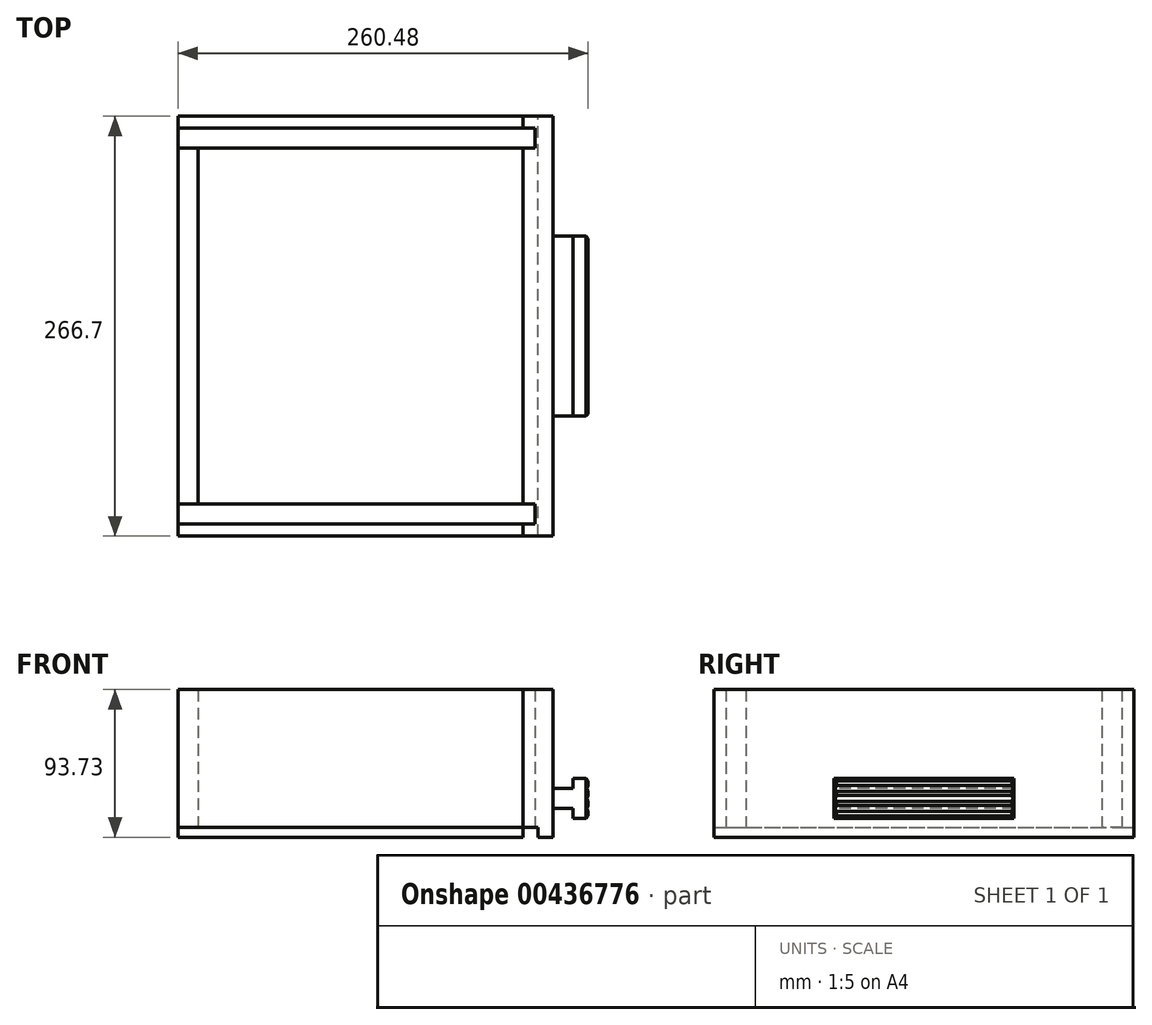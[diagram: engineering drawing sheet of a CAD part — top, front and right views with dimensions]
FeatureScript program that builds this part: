
annotation { "Feature Type Name" : "Feature", "Feature Type Description" : "" }
export const myFeature = defineFeature(function(context is Context, id is Id, definition is map)
    precondition{}
    {
        {
            var Q0;
            Q0=qCreatedBy(makeId("Top.planeOp"),FACE);
            var sketch = newSketch(context, id + "F0", { "sketchPlane" : qUnion([Q0])});
            skLineSegment(sketch, "E0.bottom", {"start": v(114.3, -133.35) * mm, "end": v(-114.3, -133.35) * mm});
            skLineSegment(sketch, "E0.top", {"start": v(114.3, 133.35) * mm, "end": v(-114.3, 133.35) * mm});
            skLineSegment(sketch, "E0.left", {"start": v(114.3, -133.35) * mm, "end": v(114.3, 133.35) * mm});
            skLineSegment(sketch, "E0.right", {"start": v(-114.3, -133.35) * mm, "end": v(-114.3, 133.35) * mm});
            skPoint(sketch, "E0.middle", {"position": v(0, 0) * mm});
            skSolve(sketch);
        }
        {
            var Q0;
            Q0 = qSketchRegion(id + "F0", true);
            extrude(context, id + "F1", {"entities" : qUnion([Q0]), "depth" : 6.35 * mm});
        }
        {
            var Q0;
            Q0=makeQuery(id+"F1.opExtrude","SWEPT_FACE",FACE,{"disambiguationData":[OSD([sQuery(id+"F0.wireOp",EDGE,"E0.left")])]});
            var sketch = newSketch(context, id + "F2", { "sketchPlane" : qUnion([Q0])});
            skLineSegment(sketch, "E1.bottom", {"start": v(-133.35, 0) * mm, "end": v(133.35, 0) * mm});
            skLineSegment(sketch, "E1.top", {"start": v(-133.35, 93.73) * mm, "end": v(133.35, 93.73) * mm});
            skLineSegment(sketch, "E1.left", {"start": v(-133.35, 0) * mm, "end": v(-133.35, 93.73) * mm});
            skLineSegment(sketch, "E1.right", {"start": v(133.35, 0) * mm, "end": v(133.35, 93.73) * mm});
            skSolve(sketch);
        }
        {
            var Q0;
            Q0 = qSketchRegion(id + "F2", true);
            extrude(context, id + "F3", {"entities" : qUnion([Q0]), "endBound" : BoundingType.SYMMETRIC, "depth" : 19.05 * mm});
        }
        {
            var Q0;
            Q0=makeQuery(id+"F3.opExtrude","CAP_FACE",FACE,{"disambiguationData":[OSD([sQuery(id+"F2.wireOp",EDGE,"E1.bottom"),sQuery(id+"F2.wireOp",EDGE,"E1.top"),sQuery(id+"F2.wireOp",EDGE,"E1.left"),sQuery(id+"F2.wireOp",EDGE,"E1.right")])],"isStart":true});
            var sketch = newSketch(context, id + "F4", { "sketchPlane" : qUnion([Q0])});
            skLineSegment(sketch, "E2.bottom", {"start": v(-125.73, 93.73) * mm, "end": v(-113.03, 93.73) * mm});
            skLineSegment(sketch, "E2.top", {"start": v(-125.73, 6.35) * mm, "end": v(-113.03, 6.35) * mm});
            skLineSegment(sketch, "E2.left", {"start": v(-125.73, 93.73) * mm, "end": v(-125.73, 6.35) * mm});
            skLineSegment(sketch, "E2.right", {"start": v(-113.03, 93.73) * mm, "end": v(-113.03, 6.35) * mm});
            skLineSegment(sketch, "E3.bottom", {"start": v(125.73, 93.73) * mm, "end": v(113.03, 93.73) * mm});
            skLineSegment(sketch, "E3.top", {"start": v(125.73, 6.35) * mm, "end": v(113.03, 6.35) * mm});
            skLineSegment(sketch, "E3.left", {"start": v(125.73, 93.73) * mm, "end": v(125.73, 6.35) * mm});
            skLineSegment(sketch, "E3.right", {"start": v(113.03, 93.73) * mm, "end": v(113.03, 6.35) * mm});
            skSolve(sketch);
        }
        {
            var Q0;
            Q0=makeQuery(id+"F4.imprint","IMPRINT",FACE,{"disambiguationData":[TD([[makeQuery(id+"F4.imprint","IMPRINT",EDGE,{"derivedFrom":sQuery(id+"F4.wireOp",EDGE,"E2.bottom")}),1.0]])]});
            var Q1;
            Q1=makeQuery(id+"F4.imprint","IMPRINT",FACE,{"disambiguationData":[TD([[makeQuery(id+"F4.imprint","IMPRINT",EDGE,{"derivedFrom":sQuery(id+"F4.wireOp",EDGE,"E3.bottom")}),1.0]])]});
            extrude(context, id + "F5", {"entities" : qUnion([Q0, Q1]), "operationType" : NewBodyOperationType.REMOVE, "oppositeDirection" : true, "depth" : 7.62 * mm});
        }
        {
            var Q0;
            Q0=makeQuery(id+"F3.opExtrude","SWEPT_FACE",FACE,{"disambiguationData":[OSD([sQuery(id+"F2.wireOp",EDGE,"E1.right")])]});
            var sketch = newSketch(context, id + "F6", { "sketchPlane" : qUnion([Q0])});
            skLineSegment(sketch, "E4.bottom", {"start": v(-114.3, 0) * mm, "end": v(-104.78, 0) * mm});
            skLineSegment(sketch, "E4.top", {"start": v(-114.3, 6.35) * mm, "end": v(-104.78, 6.35) * mm});
            skLineSegment(sketch, "E4.left", {"start": v(-114.3, 0) * mm, "end": v(-114.3, 6.35) * mm});
            skLineSegment(sketch, "E4.right", {"start": v(-104.78, 0) * mm, "end": v(-104.78, 6.35) * mm});
            skSolve(sketch);
        }
        {
            var Q0;
            Q0 = qSketchRegion(id + "F6", true);
            extrude(context, id + "F7", {"entities" : qUnion([Q0]), "operationType" : NewBodyOperationType.REMOVE, "endBound" : BoundingType.THROUGH_ALL, "oppositeDirection" : true, "depth" : 25.4 * mm});
        }
        {
            var Q0;
            Q0=makeQuery(id+"F5.boolean.opBoolean","COPY",FACE,{"derivedFrom":makeQuery(id+"F5.opExtrude","CAP_FACE",FACE,{"disambiguationData":[OSD([sQuery(id+"F4.wireOp",EDGE,"E2.bottom"),sQuery(id+"F4.wireOp",EDGE,"E2.top"),sQuery(id+"F4.wireOp",EDGE,"E2.left"),sQuery(id+"F4.wireOp",EDGE,"E2.right")])],"isStart":false})});
            var Q1;
            Q1=makeQuery(id+"F5.boolean.opBoolean","COPY",FACE,{"derivedFrom":makeQuery(id+"F5.opExtrude","CAP_FACE",FACE,{"disambiguationData":[OSD([sQuery(id+"F4.wireOp",EDGE,"E3.bottom"),sQuery(id+"F4.wireOp",EDGE,"E3.top"),sQuery(id+"F4.wireOp",EDGE,"E3.left"),sQuery(id+"F4.wireOp",EDGE,"E3.right")])],"isStart":false})});
            var Q2;
            Q2=makeQuery(id+"F1.opExtrude","SWEPT_FACE",FACE,{"disambiguationData":[OSD([sQuery(id+"F0.wireOp",EDGE,"E0.right")])]});
            extrude(context, id + "F8", {"entities" : qUnion([Q0, Q1]), "endBound" : BoundingType.UP_TO_SURFACE, "endBoundEntityFace" : qUnion([Q2]), "depth" : 25.4 * mm});
        }
        {
            var Q0;
            Q0=makeQuery(id+"F8.opExtrude","CAP_FACE",FACE,{"disambiguationData":[OSD([sQuery(id+"F4.wireOp",EDGE,"E2.bottom"),sQuery(id+"F4.wireOp",EDGE,"E2.top"),sQuery(id+"F4.wireOp",EDGE,"E2.left"),sQuery(id+"F4.wireOp",EDGE,"E2.right")])],"isStart":false});
            var sketch = newSketch(context, id + "F9", { "sketchPlane" : qUnion([Q0])});
            skLineSegment(sketch, "E5.bottom", {"start": v(-113.03, 6.35) * mm, "end": v(113.03, 6.35) * mm});
            skLineSegment(sketch, "E5.top", {"start": v(-113.03, 93.73) * mm, "end": v(113.03, 93.73) * mm});
            skLineSegment(sketch, "E5.left", {"start": v(-113.03, 6.35) * mm, "end": v(-113.03, 93.73) * mm});
            skLineSegment(sketch, "E5.right", {"start": v(113.03, 6.35) * mm, "end": v(113.03, 93.73) * mm});
            skLineSegment(sketch, "E6.0", {"start": v(113.03, 93.73) * mm, "end": v(113.03, 6.35) * mm});
            skSolve(sketch);
        }
        {
            var Q0;
            Q0 = qSketchRegion(id + "F9", true);
            extrude(context, id + "F10", {"entities" : qUnion([Q0]), "oppositeDirection" : true, "depth" : 12.7 * mm});
        }
        {
            var Q0;
            Q0=makeQuery(id+"F3.opExtrude","SWEPT_FACE",FACE,{"disambiguationData":[OSD([sQuery(id+"F2.wireOp",EDGE,"E1.left")])]});
            cPlane(context, id + "F11", {"entities" : qUnion([Q0]), "cplaneType" : CPlaneType.OFFSET, "offset" : 76.2 * mm, "oppositeDirection" : true, "width" : 152.4 * mm, "height" : 152.4 * mm});
        }
        {
            var Q0;
            Q0=qCreatedBy(id+"F11.planeOp",FACE);
            var sketch = newSketch(context, id + "F12", { "sketchPlane" : qUnion([Q0])});
            skLineSegment(sketch, "E7.0", {"start": v(123.82, 93.73) * mm, "end": v(123.82, 0) * mm});
            skLineSegment(sketch, "E8.bottom", {"start": v(123.82, 18.29) * mm, "end": v(136.52, 18.29) * mm});
            skLineSegment(sketch, "E8.top", {"start": v(123.82, 30.99) * mm, "end": v(136.52, 30.99) * mm});
            skLineSegment(sketch, "E8.left", {"start": v(123.82, 18.29) * mm, "end": v(123.82, 30.99) * mm});
            skLineSegment(sketch, "E8.right", {"start": v(136.52, 18.29) * mm, "end": v(136.52, 30.99) * mm});
            skLineSegment(sketch, "E9.bottom", {"start": v(136.52, 11.94) * mm, "end": v(146.18, 11.94) * mm});
            skLineSegment(sketch, "E9.top", {"start": v(136.52, 37.34) * mm, "end": v(146.18, 37.34) * mm});
            skLineSegment(sketch, "E9.left", {"start": v(136.52, 11.94) * mm, "end": v(136.52, 37.34) * mm});
            skLineSegment(sketch, "E9.right", {"start": v(146.18, 11.94) * mm, "end": v(146.18, 37.34) * mm});
            skSolve(sketch);
        }
        {
            var Q0;
            Q0 = qSketchRegion(id + "F12", true);
            extrude(context, id + "F13", {"entities" : qUnion([Q0]), "oppositeDirection" : true, "depth" : 114.3 * mm});
        }
        {
            var Q0;
            Q0=makeQuery(id+"F13.opExtrude","SWEPT_FACE",FACE,{"disambiguationData":[OSD([sQuery(id+"F12.wireOp",EDGE,"E9.right")])]});
            chamfer(context, id + "F14", {"entities" : qUnion([Q0]), "width" : 1.52 * mm, "tangentPropagation" : true});
        }
        {
            var Q0;
            Q0=makeQuery(id+"F13.opExtrude","CAP_FACE",FACE,{"disambiguationData":[OSD([sQuery(id+"F12.wireOp",EDGE,"E8.bottom"),sQuery(id+"F12.wireOp",EDGE,"E8.top"),sQuery(id+"F12.wireOp",EDGE,"E8.left"),sQuery(id+"F12.wireOp",EDGE,"E9.bottom"),sQuery(id+"F12.wireOp",EDGE,"E9.top"),sQuery(id+"F12.wireOp",EDGE,"E9.left"),sQuery(id+"F12.wireOp",EDGE,"E9.right")])],"isStart":true});
            var sketch = newSketch(context, id + "F15", { "sketchPlane" : qUnion([Q0])});
            skLineSegment(sketch, "E10.0", {"start": v(146.18, 35.81) * mm, "end": v(146.18, 13.46) * mm});
            skCircle(sketch, "E11", {"center": v(148.72, 30.99) * mm, "radius": 3.18 * mm});
            skCircle(sketch, "E12", {"center": v(148.72, 24.64) * mm, "radius": 3.18 * mm});
            skCircle(sketch, "E13", {"center": v(148.72, 18.29) * mm, "radius": 3.18 * mm});
            skSolve(sketch);
        }
        {
            var Q0;
            Q0 = qSketchRegion(id + "F15", true);
            extrude(context, id + "F16", {"entities" : qUnion([Q0]), "operationType" : NewBodyOperationType.REMOVE, "endBound" : BoundingType.THROUGH_ALL, "oppositeDirection" : true, "depth" : 25.4 * mm});
        }
    });
